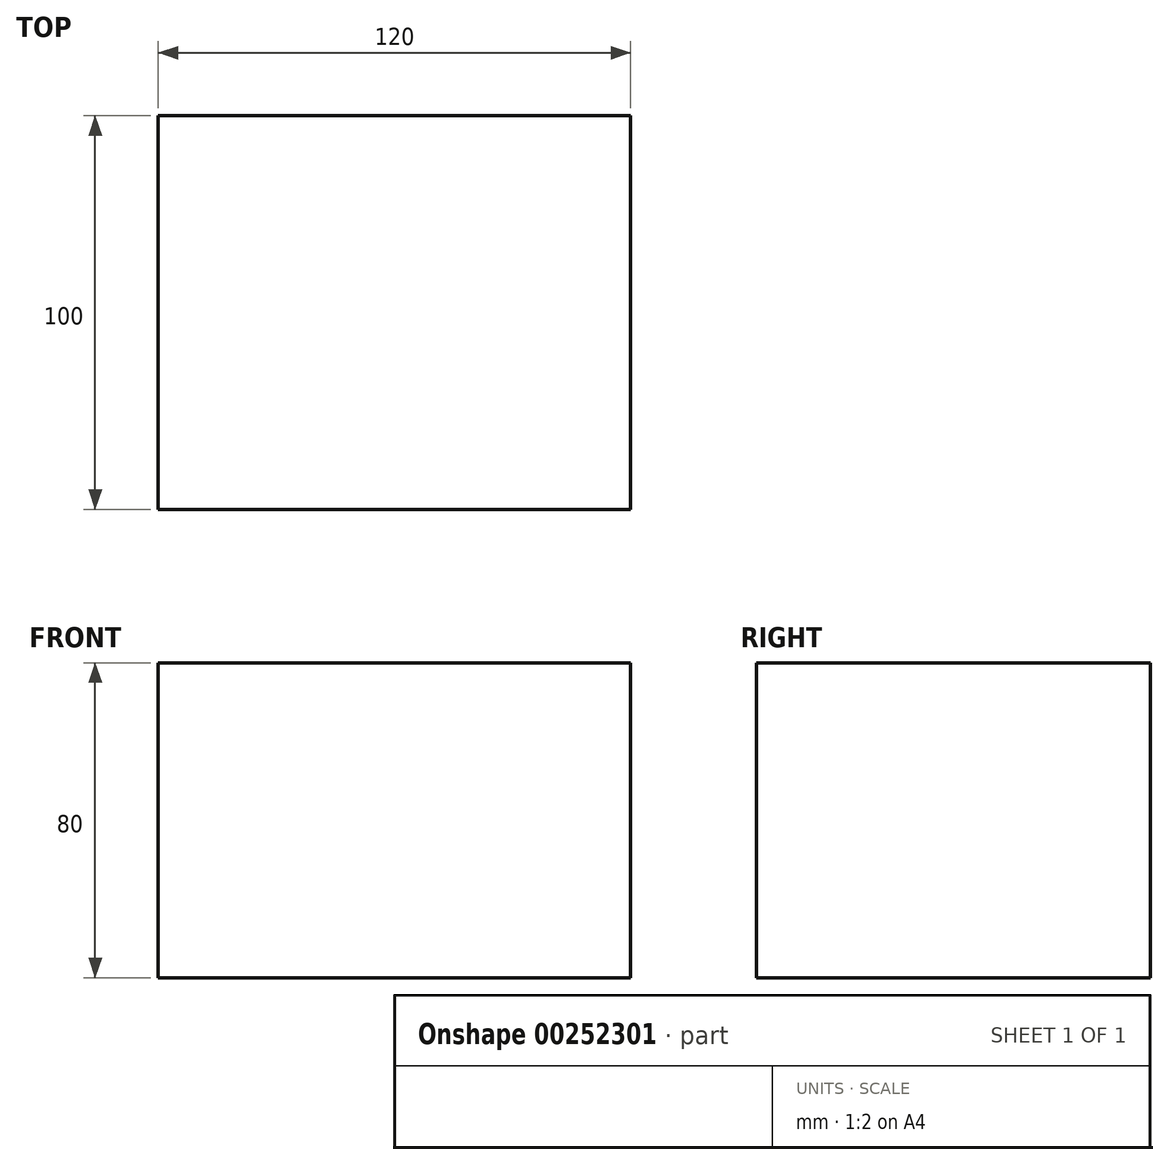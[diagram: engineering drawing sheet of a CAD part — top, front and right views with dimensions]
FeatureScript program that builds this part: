
annotation { "Feature Type Name" : "Feature", "Feature Type Description" : "" }
export const myFeature = defineFeature(function(context is Context, id is Id, definition is map)
    precondition{}
    {
        {
            var Q0;
            Q0=qCreatedBy(makeId("Front.planeOp"),FACE);
            var sketch = newSketch(context, id + "F0", { "sketchPlane" : qUnion([Q0])});
            skLineSegment(sketch, "E0.bottom", {"start": v(-60, 40) * mm, "end": v(60, 40) * mm});
            skLineSegment(sketch, "E0.top", {"start": v(-60, -40) * mm, "end": v(60, -40) * mm});
            skLineSegment(sketch, "E0.left", {"start": v(-60, 40) * mm, "end": v(-60, -40) * mm});
            skLineSegment(sketch, "E0.right", {"start": v(60, 40) * mm, "end": v(60, -40) * mm});
            skPoint(sketch, "E0.middle", {"position": v(0, 0) * mm});
            skSolve(sketch);
        }
        {
            var Q0;
            Q0=makeQuery(id+"F0.imprint","IMPRINT",FACE,{"disambiguationData":[TD([[makeQuery(id+"F0.imprint","IMPRINT",EDGE,{"derivedFrom":sQuery(id+"F0.wireOp",EDGE,"E0.bottom")}),-1.0]])]});
            extrude(context, id + "F1", {"entities" : qUnion([Q0]), "endBound" : BoundingType.SYMMETRIC, "depth" : 100 * mm});
        }
    });
